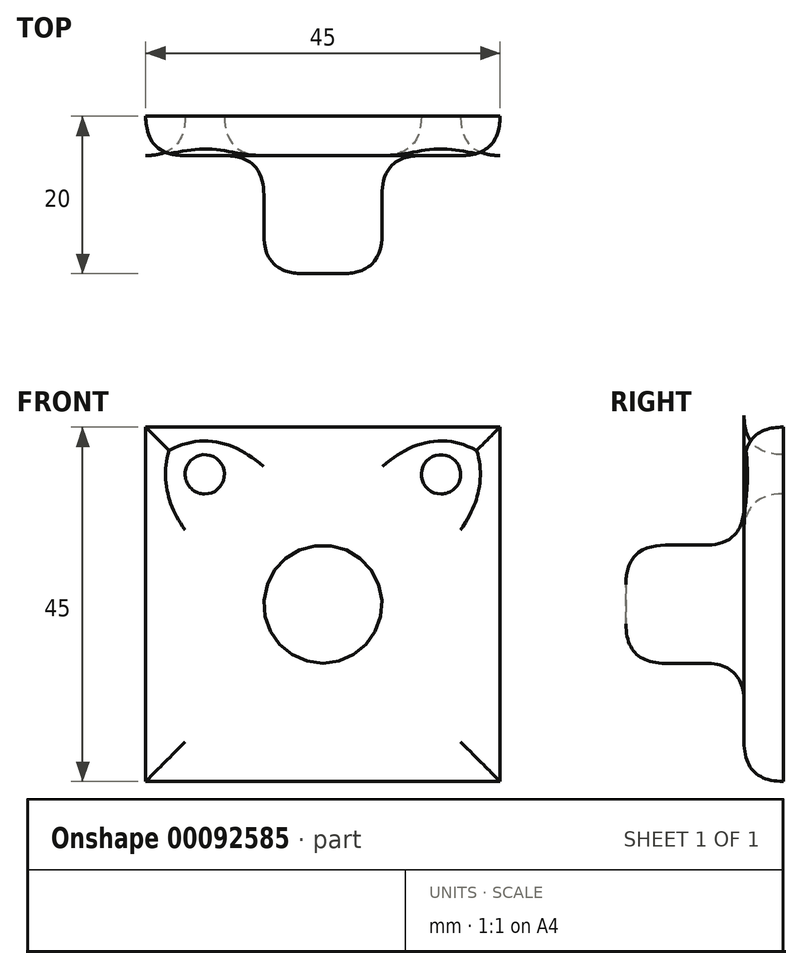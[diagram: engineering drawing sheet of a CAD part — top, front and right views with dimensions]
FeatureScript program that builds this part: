
annotation { "Feature Type Name" : "Feature", "Feature Type Description" : "" }
export const myFeature = defineFeature(function(context is Context, id is Id, definition is map)
    precondition{}
    {
        {
            var Q0;
            Q0=qCreatedBy(makeId("Front.planeOp"),FACE);
            var sketch = newSketch(context, id + "F0", { "sketchPlane" : qUnion([Q0])});
            skLineSegment(sketch, "E0", {"start": v(-25.32, 13.99) * mm, "end": v(-25.32, -31.01) * mm});
            skLineSegment(sketch, "E1", {"start": v(-25.32, -31.01) * mm, "end": v(19.68, -31.01) * mm});
            skLineSegment(sketch, "E2", {"start": v(19.68, -31.01) * mm, "end": v(19.68, 13.99) * mm});
            skLineSegment(sketch, "E3", {"start": v(19.68, 13.99) * mm, "end": v(-25.32, 13.99) * mm});
            skCircle(sketch, "E4", {"center": v(-2.82, -8.51) * mm, "radius": 7.5 * mm});
            skSolve(sketch);
        }
        {
            var Q0;
            Q0=makeQuery(id+"F0.imprint","IMPRINT",FACE,{"disambiguationData":[TD([[makeQuery(id+"F0.imprint","IMPRINT",EDGE,{"derivedFrom":sQuery(id+"F0.wireOp",EDGE,"E4")}),1.0]])]});
            extrude(context, id + "F1", {"entities" : qUnion([Q0]), "depth" : 20 * mm});
        }
        {
            var Q0;
            Q0 = qSketchRegion(id + "F0", true);
            extrude(context, id + "F2", {"entities" : qUnion([Q0]), "operationType" : NewBodyOperationType.ADD, "depth" : 5 * mm});
        }
        {
            var Q0;
            Q0=makeQuery(id+"F2.opExtrude","CAP_FACE",FACE,{"disambiguationData":[OSD([sQuery(id+"F0.wireOp",EDGE,"E0"),sQuery(id+"F0.wireOp",EDGE,"E1"),sQuery(id+"F0.wireOp",EDGE,"E2"),sQuery(id+"F0.wireOp",EDGE,"E3"),sQuery(id+"F0.wireOp",EDGE,"E4")])],"isStart":false});
            var sketch = newSketch(context, id + "F3", { "sketchPlane" : qUnion([Q0])});
            skCircle(sketch, "E5", {"center": v(-17.82, 7.99) * mm, "radius": 2.5 * mm});
            skCircle(sketch, "E6", {"center": v(12.18, 7.99) * mm, "radius": 2.5 * mm});
            skSolve(sketch);
        }
        {
            var Q0;
            Q0=makeQuery(id+"F3.imprint","IMPRINT",FACE,{"disambiguationData":[TD([[makeQuery(id+"F3.imprint","IMPRINT",EDGE,{"derivedFrom":sQuery(id+"F3.wireOp",EDGE,"E6")}),1.0]])]});
            var Q1;
            Q1=makeQuery(id+"F3.imprint","IMPRINT",FACE,{"disambiguationData":[TD([[makeQuery(id+"F3.imprint","IMPRINT",EDGE,{"derivedFrom":sQuery(id+"F3.wireOp",EDGE,"E5")}),1.0]])]});
            extrude(context, id + "F4", {"entities" : qUnion([Q0, Q1]), "operationType" : NewBodyOperationType.REMOVE, "oppositeDirection" : true, "depth" : 25 * mm});
        }
        {
            var Q0;
            Q0=makeQuery(id+"F2.opExtrude","CAP_FACE",FACE,{"disambiguationData":[OSD([sQuery(id+"F0.wireOp",EDGE,"E0"),sQuery(id+"F0.wireOp",EDGE,"E1"),sQuery(id+"F0.wireOp",EDGE,"E2"),sQuery(id+"F0.wireOp",EDGE,"E3"),sQuery(id+"F0.wireOp",EDGE,"E4")])],"isStart":false});
            var Q1;
            Q1=makeQuery(id+"F1.opExtrude","SWEPT_FACE",FACE,{"disambiguationData":[OSD([sQuery(id+"F0.wireOp",EDGE,"E4")])]});
            fillet(context, id + "F5", {"entities" : qUnion([Q0, Q1]), "radius" : 5 * mm, "tangentPropagation" : true, "rho" : 0.5, "crossSection" : FilletCrossSection.CONIC, "allowEdgeOverflow" : false});
        }
    });
